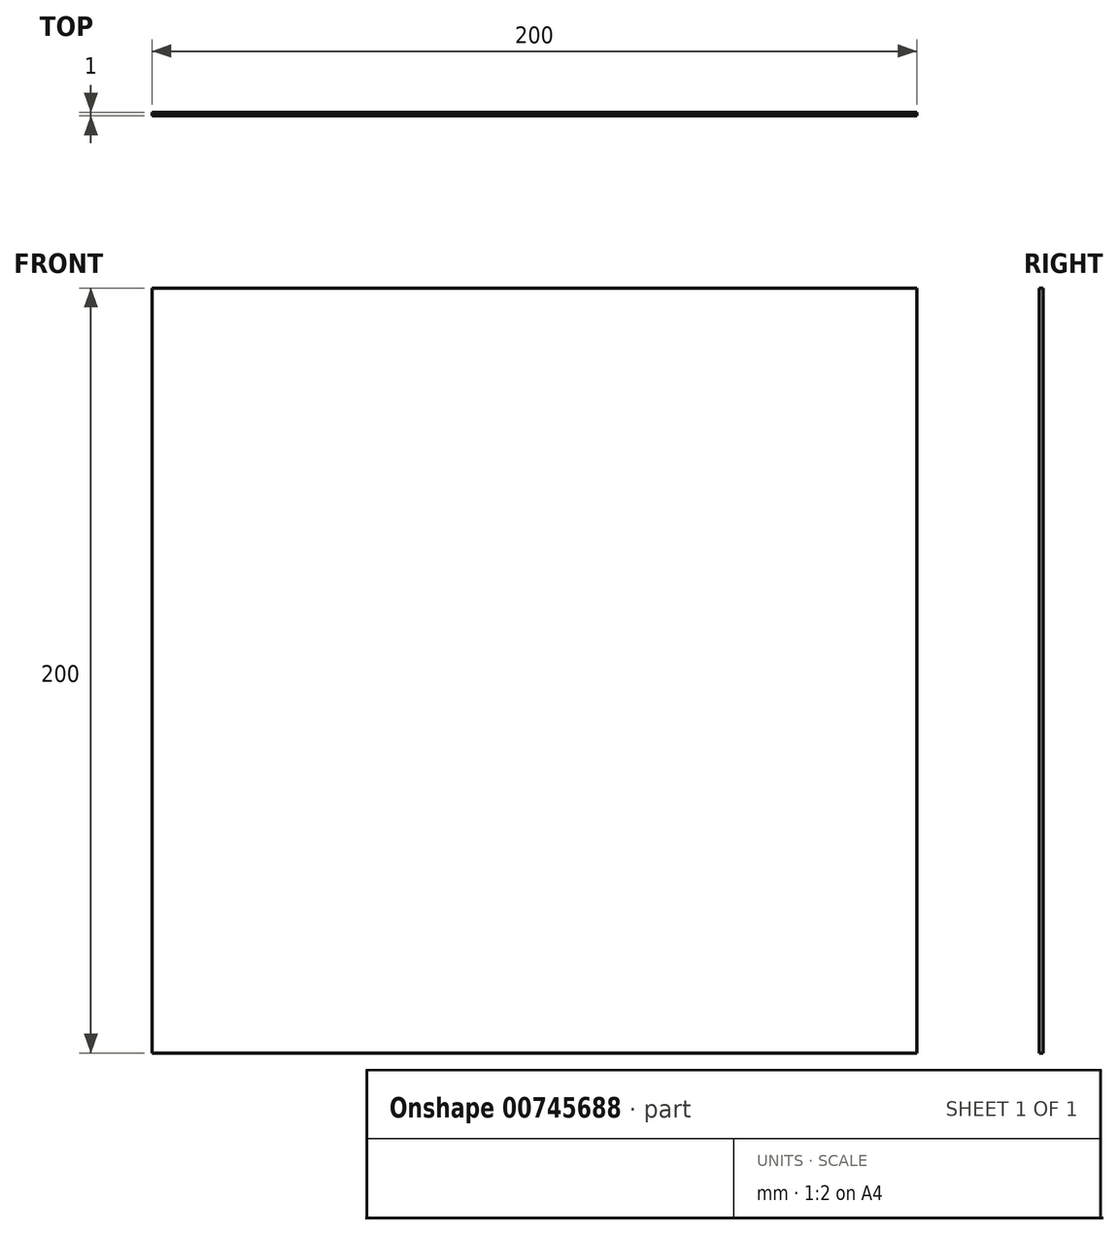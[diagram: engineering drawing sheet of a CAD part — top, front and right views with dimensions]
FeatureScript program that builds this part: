
annotation { "Feature Type Name" : "Feature", "Feature Type Description" : "" }
export const myFeature = defineFeature(function(context is Context, id is Id, definition is map)
    precondition{}
    {
        {
            var Q0;
            Q0=qCreatedBy(makeId("Front.planeOp"),FACE);
            var sketch = newSketch(context, id + "F0", { "sketchPlane" : qUnion([Q0])});
            skLineSegment(sketch, "E0.bottom", {"start": v(100, -102.38) * mm, "end": v(-100, -102.38) * mm});
            skLineSegment(sketch, "E0.top", {"start": v(100, 97.62) * mm, "end": v(-100, 97.62) * mm});
            skLineSegment(sketch, "E0.left", {"start": v(100, -102.38) * mm, "end": v(100, 97.62) * mm});
            skLineSegment(sketch, "E0.right", {"start": v(-100, -102.38) * mm, "end": v(-100, 97.62) * mm});
            skPoint(sketch, "E0.middle", {"position": v(0, -2.38) * mm});
            skSolve(sketch);
        }
        {
            var Q0;
            Q0 = qSketchRegion(id + "F0", true);
            extrude(context, id + "F1", {"entities" : qUnion([Q0]), "depth" : 1 * mm, "offsetDistance" : 25.4 * mm});
        }
    });
